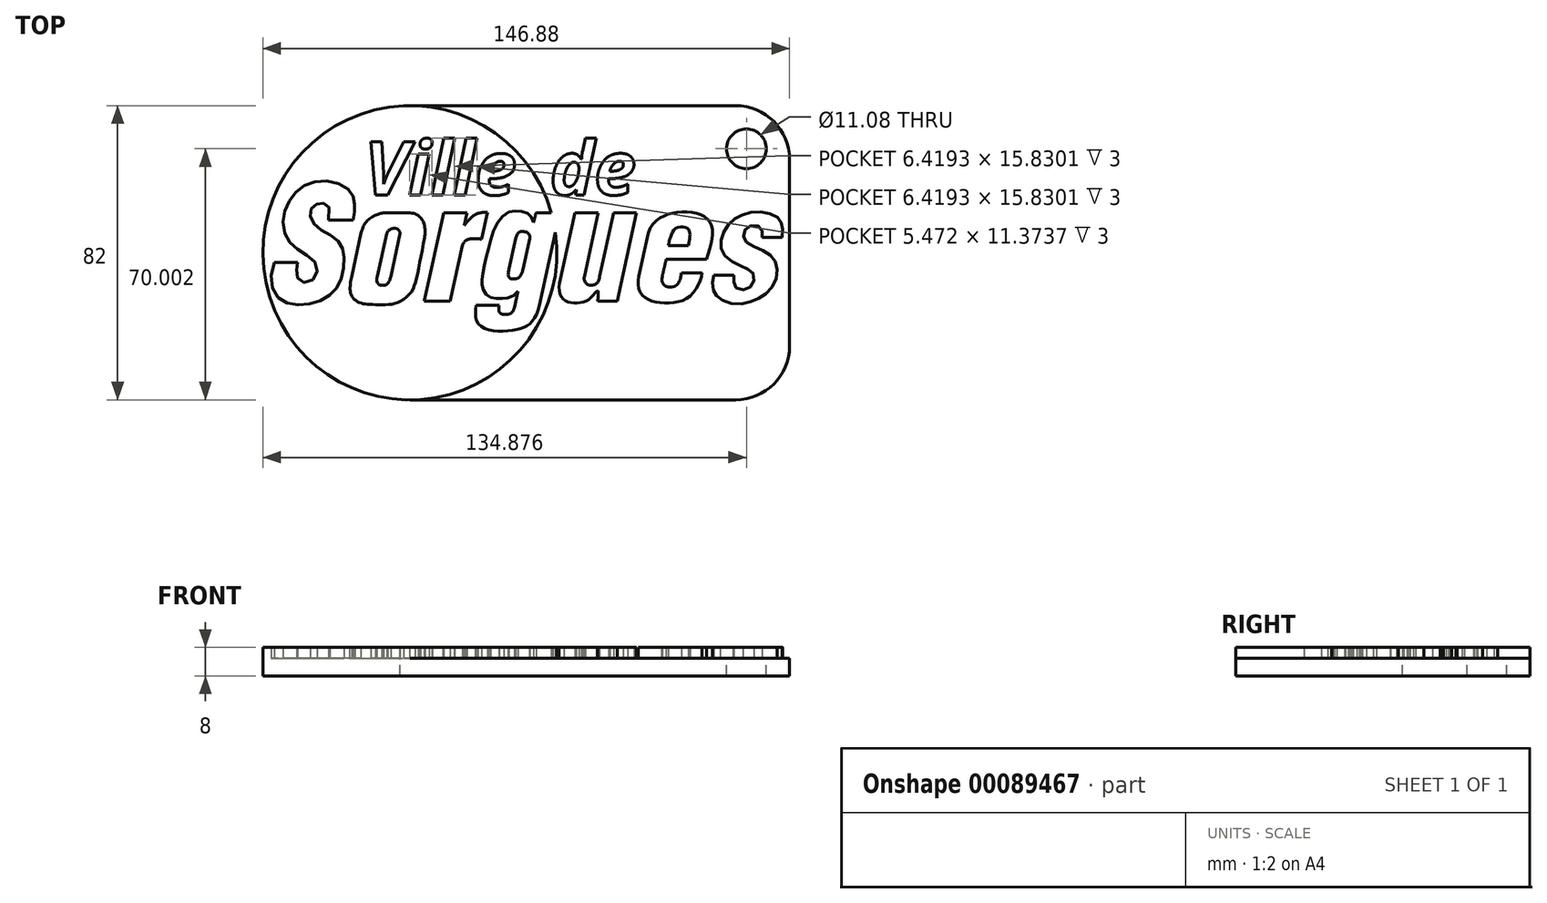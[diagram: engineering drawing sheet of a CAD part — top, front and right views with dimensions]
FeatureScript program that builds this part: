
annotation { "Feature Type Name" : "Feature", "Feature Type Description" : "" }
export const myFeature = defineFeature(function(context is Context, id is Id, definition is map)
    precondition{}
    {
        {
            var Q0;
            Q0=qCreatedBy(makeId("Top.planeOp"),FACE);
            var sketch = newSketch(context, id + "F0", { "sketchPlane" : qUnion([Q0])});
            skCircle(sketch, "E0", {"center": v(-30.87, 6.6) * mm, "radius": 41 * mm});
            skLineSegment(sketch, "E1", {"start": v(-46.68, 15.72) * mm, "end": v(-53.55, 15.72) * mm});
            skFitSpline(sketch, "E2", {"points": [v(-53.55, 15.72) * mm, v(-55.37, 20.45) * mm, v(-58.38, 18.72) * mm, v(-57.47, 14.47) * mm, v(-51.06, 10.07) * mm, v(-49.23, 4.58) * mm, v(-51.4, -3.41) * mm, v(-58.74, -7.62) * mm, v(-67.28, -6.17) * mm, v(-68.7, 3.91) * mm], "startDerivative": vector(30.5, 116.33) * mm, "endDerivative": vector(37.1, 85.72) * mm});
            skFitSpline(sketch, "E3", {"points": [v(-62.2, 3.91) * mm, v(-62.44, 1.12) * mm, v(-61.32, -1.4) * mm, v(-57.63, -0.75) * mm, v(-57.02, 3.45) * mm, v(-61, 6.77) * mm, v(-64.78, 10.13) * mm, v(-66.22, 15.64) * mm, v(-64.36, 21.2) * mm, v(-60.67, 25.07) * mm, v(-54.78, 26.66) * mm, v(-48.53, 24.7) * mm, v(-46.51, 21.77) * mm, v(-46.24, 18.72) * mm, v(-46.68, 15.72) * mm], "startDerivative": vector(-8.44, -44.96) * mm, "endDerivative": vector(-12.62, -61.68) * mm});
            skLineSegment(sketch, "E4", {"start": v(-68.7, 3.91) * mm, "end": v(-62.2, 3.91) * mm});
            skFitSpline(sketch, "E5", {"points": [v(-44.48, 12.03) * mm, v(-41.97, 16.18) * mm, v(-39.42, 17.46) * mm, v(-37.1, 17.75) * mm], "startDerivative": vector(4.21, 16.77) * mm, "endDerivative": vector(10.42, 0) * mm});
            skLineSegment(sketch, "E6", {"start": v(-44.48, 12.03) * mm, "end": v(-47.1, 0) * mm});
            skFitSpline(sketch, "E7", {"points": [v(-47.1, 0) * mm, v(-47.52, -2.89) * mm, v(-47.1, -5.39) * mm, v(-44.86, -7.3) * mm, v(-40.48, -7.86) * mm], "startDerivative": vector(-2.9, -11.48) * mm, "endDerivative": vector(16.85, 0) * mm});
            skLineSegment(sketch, "E8", {"start": v(-37.1, 17.75) * mm, "end": v(-31.46, 17.75) * mm});
            skFitSpline(sketch, "E9", {"points": [v(-31.46, 17.75) * mm, v(-28.52, 16.96) * mm, v(-27.19, 15.35) * mm, v(-26.63, 12.9) * mm, v(-26.77, 10.94) * mm], "startDerivative": vector(16.23, 0) * mm, "endDerivative": vector(-1.15, -8.28) * mm});
            skFitSpline(sketch, "E10", {"points": [v(-40.48, -7.86) * mm, v(-36.84, -7.86) * mm, v(-33.76, -7.04) * mm, v(-30.62, -4.52) * mm, v(-29, -0.53) * mm, v(-26.77, 10.94) * mm], "startDerivative": vector(21.93, -0.87) * mm, "endDerivative": vector(7.65, 42.34) * mm});
            skLineSegment(sketch, "E11", {"start": v(-39.95, 0) * mm, "end": v(-37.33, 12.03) * mm});
            skLineSegment(sketch, "E12", {"start": v(-33.58, 12.03) * mm, "end": v(-36.2, 0) * mm});
            skFitSpline(sketch, "E13", {"points": [v(-37.33, 12.03) * mm, v(-35.63, 13.36) * mm, v(-34.25, 13.16) * mm, v(-33.58, 12.03) * mm, v(-34.59, 11.23) * mm], "startDerivative": vector(4.06, 9.82) * mm, "endDerivative": vector(-5.98, -2.84) * mm});
            skFitSpline(sketch, "E14", {"points": [v(-39.95, 0) * mm, v(-39.5, -2.22) * mm, v(-37.71, -2.37) * mm, v(-36.65, -1.41) * mm, v(-36.2, 0) * mm], "startDerivative": vector(-2.91, -13) * mm, "endDerivative": vector(2.14, 8.95) * mm});
            skLineSegment(sketch, "E15", {"start": v(-26.8, -6.84) * mm, "end": v(-21.45, 17.75) * mm});
            skLineSegment(sketch, "E16", {"start": v(-21.45, 17.75) * mm, "end": v(-14.91, 17.75) * mm});
            skLineSegment(sketch, "E17", {"start": v(-14.91, 17.75) * mm, "end": v(-15.68, 14.23) * mm});
            skLineSegment(sketch, "E18", {"start": v(-26.8, -6.84) * mm, "end": v(-19.58, -6.84) * mm});
            skLineSegment(sketch, "E19", {"start": v(-19.58, -6.84) * mm, "end": v(-16.19, 8.72) * mm});
            skLineSegment(sketch, "E20", {"start": v(-10.86, 10.4) * mm, "end": v(-9.23, 17.89) * mm});
            skFitSpline(sketch, "E21", {"points": [v(-15.68, 14.23) * mm, v(-13.66, 16.46) * mm, v(-11.76, 17.62) * mm, v(-9.23, 17.89) * mm], "startDerivative": vector(5.4, 7.42) * mm, "endDerivative": vector(8.1, 0.22) * mm});
            skFitSpline(sketch, "E22", {"points": [v(-16.19, 8.72) * mm, v(-14.96, 10.15) * mm, v(-12.9, 10.55) * mm, v(-10.86, 10.4) * mm], "startDerivative": vector(3.02, 5.92) * mm, "endDerivative": vector(6.03, -0.64) * mm});
            skLineSegment(sketch, "E23", {"start": v(-3.2, 2.04) * mm, "end": v(-1.33, 10.61) * mm});
            skLineSegment(sketch, "E24", {"start": v(0.7, 2.04) * mm, "end": v(2.57, 10.61) * mm});
            skLineSegment(sketch, "E25", {"start": v(-0.74, -4.05) * mm, "end": v(-1.78, -8.83) * mm});
            skLineSegment(sketch, "E26", {"start": v(-12.33, -8) * mm, "end": v(-5.95, -8) * mm});
            skLineSegment(sketch, "E27", {"start": v(4.33, 17.75) * mm, "end": v(10.93, 17.75) * mm});
            skLineSegment(sketch, "E28", {"start": v(5.3, -8.04) * mm, "end": v(10.93, 17.75) * mm});
            skFitSpline(sketch, "E29", {"points": [v(-1.33, 10.61) * mm, v(-0.46, 12.23) * mm, v(0.86, 12.5) * mm, v(2.15, 12) * mm, v(2.59, 11.3) * mm, v(2.57, 10.61) * mm], "startDerivative": vector(1.37, 8.18) * mm, "endDerivative": vector(-0.73, -5.78) * mm});
            skFitSpline(sketch, "E30", {"points": [v(-3.2, 2.04) * mm, v(-3.44, 0.57) * mm, v(-3.2, -0.27) * mm, v(-2.17, -0.7) * mm, v(-0.65, -0.45) * mm, v(0.16, 0.48) * mm, v(0.4, 1.08) * mm, v(0.7, 2.04) * mm], "startDerivative": vector(-1.15, -6.79) * mm, "endDerivative": vector(2.21, 10.53) * mm});
            skFitSpline(sketch, "E31", {"points": [v(3.62, 15.02) * mm, v(2.53, 17.2) * mm, v(0, 18.19) * mm, v(-3.05, 18) * mm, v(-6.5, 14.88) * mm, v(-8.72, 8.69) * mm, v(-10.1, 3.25) * mm, v(-10.75, -0.82) * mm, v(-10.61, -2.76) * mm, v(-9.79, -4.72) * mm, v(-8.01, -5.97) * mm, v(-5.46, -6.16) * mm, v(-3.18, -5.86) * mm, v(-0.74, -4.05) * mm, v(-0.54, -3.09) * mm], "startDerivative": vector(-11.94, 38.07) * mm, "endDerivative": vector(-16.26, -31.54) * mm});
            skFitSpline(sketch, "E32", {"points": [v(-5.95, -8) * mm, v(-5.65, -10.26) * mm, v(-2.62, -10.2) * mm, v(-1.78, -8.83) * mm], "startDerivative": vector(-0.6, -8.06) * mm, "endDerivative": vector(1.49, 4.6) * mm});
            skFitSpline(sketch, "E33", {"points": [v(-12.33, -8) * mm, v(-12.33, -12.1) * mm, v(-9.84, -14.59) * mm, v(-3.98, -15.22) * mm, v(0.78, -14.25) * mm, v(3.2, -12.62) * mm, v(5.3, -8.04) * mm], "startDerivative": vector(-3.82, -23) * mm, "endDerivative": vector(7.38, 32.85) * mm});
            skFitSpline(sketch, "E34", {"points": [v(3.62, 15.02) * mm, v(4.33, 17.75) * mm], "startDerivative": vector(0.71, 2.5) * mm, "endDerivative": vector(0.71, 2.5) * mm});
            skPoint(sketch, "E35.orphan", {"position": v(11.99, 17.75) * mm});
            skLineSegment(sketch, "E36", {"start": v(15.2, 17.75) * mm, "end": v(21.67, 17.75) * mm});
            skPoint(sketch, "E36.startSnap0", {"position": v(7.63, 17.75) * mm});
            skLineSegment(sketch, "E37", {"start": v(25.94, 17.75) * mm, "end": v(32.3, 17.75) * mm});
            skLineSegment(sketch, "E38", {"start": v(21.5, -6.84) * mm, "end": v(26.94, -6.84) * mm});
            skPoint(sketch, "E38.startSnap0", {"position": v(-23.2, -6.84) * mm});
            skPoint(sketch, "E38.endSnap0", {"position": v(-23.2, -6.84) * mm});
            skLineSegment(sketch, "E39", {"start": v(40.62, 4.75) * mm, "end": v(51.92, 4.75) * mm});
            skLineSegment(sketch, "E40", {"start": v(41.22, 8.6) * mm, "end": v(46.8, 8.6) * mm});
            skLineSegment(sketch, "E41", {"start": v(15.2, 17.75) * mm, "end": v(10.91, -1.96) * mm});
            skLineSegment(sketch, "E42", {"start": v(21.67, 17.75) * mm, "end": v(17.8, 0) * mm});
            skLineSegment(sketch, "E43", {"start": v(25.94, 17.75) * mm, "end": v(22.07, 0) * mm});
            skLineSegment(sketch, "E44", {"start": v(32.3, 17.75) * mm, "end": v(26.94, -6.84) * mm});
            skLineSegment(sketch, "E45", {"start": v(35.56, 12.03) * mm, "end": v(32.94, 0) * mm});
            skFitSpline(sketch, "E46", {"points": [v(10.91, -1.96) * mm, v(11.94, -6.38) * mm, v(15.88, -7.4) * mm, v(19.48, -6.04) * mm, v(21.49, -4.03) * mm, v(21.5, -6.84) * mm], "startDerivative": vector(-4.87, -23.72) * mm, "endDerivative": vector(-3.5, -25.24) * mm});
            skFitSpline(sketch, "E47", {"points": [v(17.8, 0) * mm, v(18.89, -2.31) * mm, v(21.01, -2.1) * mm, v(22.07, 0) * mm], "startDerivative": vector(-2.23, -9) * mm, "endDerivative": vector(2.64, 10.78) * mm});
            skFitSpline(sketch, "E48", {"points": [v(35.56, 12.03) * mm, v(38.42, 15.94) * mm, v(41.6, 17.5) * mm, v(46.13, 18.02) * mm, v(50.22, 17.24) * mm, v(52.65, 15.32) * mm, v(53.55, 12.03) * mm, v(51.92, 4.75) * mm], "startDerivative": vector(8, 35.37) * mm, "endDerivative": vector(-6.52, -21.66) * mm});
            skFitSpline(sketch, "E49", {"points": [v(32.94, 0) * mm, v(34.12, -5.4) * mm, v(39.94, -7.4) * mm, v(47.3, -5.45) * mm, v(50.64, 0.91) * mm, v(50.68, 3.2) * mm], "startDerivative": vector(-6.28, -31.9) * mm, "endDerivative": vector(-0.94, 14.05) * mm});
            skFitSpline(sketch, "E50", {"points": [v(39.5, 0) * mm, v(40.62, -2.78) * mm, v(43.55, -2.4) * mm, v(44.67, 0) * mm, v(44.82, 0.91) * mm], "startDerivative": vector(-3.13, -15.6) * mm, "endDerivative": vector(0.96, 6.1) * mm});
            skFitSpline(sketch, "E51", {"points": [v(41.22, 8.6) * mm, v(41.58, 10.16) * mm, v(43.3, 13.38) * mm, v(46.58, 13.3) * mm, v(47.25, 11.6) * mm, v(46.8, 8.6) * mm], "startDerivative": vector(3.23, 15.78) * mm, "endDerivative": vector(-3.17, -15.13) * mm});
            skFitSpline(sketch, "E52", {"points": [v(40.62, 4.75) * mm, v(39.5, 0) * mm], "startDerivative": vector(-1.24, -4.75) * mm, "endDerivative": vector(-1.24, -4.75) * mm});
            skPoint(sketch, "E53.orphan", {"position": v(27.12, -6.84) * mm});
            skLineSegment(sketch, "E54", {"start": v(44.82, 0.91) * mm, "end": v(50.64, 0.91) * mm});
            skFitSpline(sketch, "E55", {"points": [v(67.4, 10.9) * mm, v(67.36, 12.7) * mm, v(66.34, 14.03) * mm, v(63.7, 13.96) * mm, v(62.34, 12.46) * mm, v(62.4, 10.4) * mm, v(64.15, 8.73) * mm, v(67.92, 7.05) * mm, v(70.48, 4.99) * mm, v(71.53, 2.32) * mm, v(71.04, -1.16) * mm, v(68.92, -4.37) * mm, v(66.03, -6.31) * mm, v(62.83, -7.42) * mm, v(58.16, -7.46) * mm, v(55.3, -5.98) * mm, v(54.07, -4.45) * mm, v(53.53, -2.15) * mm, v(53.96, 0.28) * mm], "startDerivative": vector(4.71, 40.9) * mm, "endDerivative": vector(10.6, 37.94) * mm});
            skFitSpline(sketch, "E56", {"points": [v(59.53, 0.4) * mm, v(59.46, -1.73) * mm, v(60.46, -3.38) * mm, v(63.13, -3.55) * mm, v(65, -1.75) * mm, v(64.82, 0.94) * mm, v(63.17, 2.17) * mm, v(59.68, 3.72) * mm, v(56.58, 6.31) * mm, v(55.81, 9.37) * mm, v(56.82, 12.78) * mm, v(59.03, 15.48) * mm, v(61.96, 17.2) * mm, v(66.03, 18) * mm, v(70.3, 17.15) * mm, v(72.36, 15.67) * mm, v(72.98, 13.88) * mm, v(72.95, 10.9) * mm], "startDerivative": vector(-8.42, -48.12) * mm, "endDerivative": vector(-7.47, -56.36) * mm});
            skLineSegment(sketch, "E57", {"start": v(53.96, 0.28) * mm, "end": v(59.51, 0.28) * mm});
            skLineSegment(sketch, "E58", {"start": v(67.4, 10.9) * mm, "end": v(72.95, 10.9) * mm});
            skLineSegment(sketch, "E59.bottom", {"start": v(-30.87, 47.6) * mm, "end": v(75, 47.6) * mm});
            skLineSegment(sketch, "E59.top", {"start": v(-30.87, -34.4) * mm, "end": v(75, -34.4) * mm});
            skLineSegment(sketch, "E59.right", {"start": v(75, 47.6) * mm, "end": v(75, -34.4) * mm});
            skCircle(sketch, "E60", {"center": v(63, 35.6) * mm, "radius": 5.54 * mm});
            skSolve(sketch);
        }
        {
            var Q0;
            Q0=qCreatedBy(makeId("Top.planeOp"),FACE);
            var sketch = newSketch(context, id + "F1", { "sketchPlane" : qUnion([Q0])});
            skText(sketch, "E61", { "text": "Ville", "fontName": "OpenSans-BoldItalic.ttf"});
            const initialGuessF1  = {"E61": [-0.04358, 0.02272, 1, 0, 0.015]};
            skSetInitialGuess(sketch, initialGuessF1);
            skSolve(sketch);
        }
        {
            var Q0;
            Q0=qCreatedBy(makeId("Top.planeOp"),FACE);
            var sketch = newSketch(context, id + "F2", { "sketchPlane" : qUnion([Q0])});
            skText(sketch, "E62", { "text": "de", "fontName": "OpenSans-BoldItalic.ttf"});
            const initialGuessF2  = {"E62": [0.00816, 0.02275, 1, 0, 0.015]};
            skSetInitialGuess(sketch, initialGuessF2);
            skSolve(sketch);
        }
        {
            var Q0;
            Q0=makeQuery(id+"F0.imprint","IMPRINT",FACE,{"disambiguationData":[TD([[makeQuery(id+"F0.imprint","IMPRINT",EDGE,{"derivedFrom":sQuery(id+"F0.wireOp",EDGE,"E1")}),1.0]])]});
            var Q1;
            Q1=makeQuery(id+"F0.imprint","IMPRINT",FACE,{"disambiguationData":[TD([[makeQuery(id+"F0.imprint","IMPRINT",EDGE,{"derivedFrom":sQuery(id+"F0.wireOp",EDGE,"E36")}),1.0]])]});
            var Q2;
            Q2=makeQuery(id+"F0.imprint","IMPRINT",FACE,{"disambiguationData":[TD([[makeQuery(id+"F0.imprint","IMPRINT",EDGE,{"derivedFrom":sQuery(id+"F0.wireOp",EDGE,"E1")}),-1.0]])]});
            var Q3;
            Q3=makeQuery(id+"F0.imprint","IMPRINT",FACE,{"disambiguationData":[TD([[makeQuery(id+"F0.imprint","IMPRINT",EDGE,{"derivedFrom":sQuery(id+"F0.wireOp",EDGE,"E5")}),-1.0]])]});
            var Q4;
            {var subQ1=sQuery(id+"F0.wireOp",EDGE,"E11");Q4=makeQuery(id+"F0.imprint","IMPRINT",FACE,{"disambiguationData":[TD([[makeQuery(id+"F0.imprint","IMPRINT",EDGE,{"derivedFrom":subQ1}),-1.0]])]});}
            var Q5;
            Q5=makeQuery(id+"F0.imprint","IMPRINT",FACE,{"disambiguationData":[TD([[makeQuery(id+"F0.imprint","IMPRINT",EDGE,{"derivedFrom":sQuery(id+"F0.wireOp",EDGE,"E15")}),-1.0]])]});
            var Q6;
            Q6=makeQuery(id+"F0.imprint","IMPRINT",FACE,{"disambiguationData":[TD([[makeQuery(id+"F0.imprint","IMPRINT",EDGE,{"derivedFrom":sQuery(id+"F0.wireOp",EDGE,"E23")}),1.0]])]});
            var Q7;
            Q7=makeQuery(id+"F0.imprint","IMPRINT",FACE,{"disambiguationData":[TD([[makeQuery(id+"F0.imprint","IMPRINT",EDGE,{"derivedFrom":sQuery(id+"F0.wireOp",EDGE,"E23")}),-1.0]])]});
            var Q8;
            {var subQ0=sQuery(id+"F0.wireOp",EDGE,"E27");var subQ1=sQuery(id+"F0.wireOp",EDGE,"E0");var subQ2=makeQuery(id+"F0.imprint","INTERSECT",VERTEX,{"derivedFrom":[subQ1,subQ0]});Q8=makeQuery(id+"F0.imprint","IMPRINT",FACE,{"disambiguationData":[TD([[makeQuery(id+"F0.imprint","IMPRINT",EDGE,{"disambiguationData":[TD([[subQ2,1.0]])],"derivedFrom":subQ1}),-1.0]])]});}
            var Q9;
            Q9=makeQuery(id+"F0.imprint","IMPRINT",FACE,{"disambiguationData":[TD([[makeQuery(id+"F0.imprint","IMPRINT",EDGE,{"derivedFrom":sQuery(id+"F0.wireOp",EDGE,"E36")}),-1.0]])]});
            var Q10;
            Q10=makeQuery(id+"F0.imprint","IMPRINT",FACE,{"disambiguationData":[TD([[makeQuery(id+"F0.imprint","IMPRINT",EDGE,{"derivedFrom":sQuery(id+"F0.wireOp",EDGE,"E39")}),1.0]])]});
            var Q11;
            Q11=makeQuery(id+"F0.imprint","IMPRINT",FACE,{"disambiguationData":[TD([[makeQuery(id+"F0.imprint","IMPRINT",EDGE,{"derivedFrom":sQuery(id+"F0.wireOp",EDGE,"E40")}),1.0]])]});
            var Q12;
            Q12=makeQuery(id+"F0.imprint","IMPRINT",FACE,{"disambiguationData":[TD([[makeQuery(id+"F0.imprint","IMPRINT",EDGE,{"derivedFrom":sQuery(id+"F0.wireOp",EDGE,"E55")}),-1.0]])]});
            extrude(context, id + "F3", {"entities" : qUnion([Q0, Q1, Q2, Q3, Q4, Q5, Q6, Q7, Q8, Q9, Q10, Q11, Q12]), "oppositeDirection" : true, "depth" : 5 * mm});
        }
        {
            var Q0;
            Q0=makeQuery(id+"F0.imprint","IMPRINT",FACE,{"disambiguationData":[TD([[makeQuery(id+"F0.imprint","IMPRINT",EDGE,{"derivedFrom":sQuery(id+"F0.wireOp",EDGE,"E1")}),1.0]])]});
            var Q1;
            {var subQ1=sQuery(id+"F0.wireOp",EDGE,"E11");Q1=makeQuery(id+"F0.imprint","IMPRINT",FACE,{"disambiguationData":[TD([[makeQuery(id+"F0.imprint","IMPRINT",EDGE,{"derivedFrom":subQ1}),-1.0]])]});}
            var Q2;
            Q2=makeQuery(id+"F0.imprint","IMPRINT",FACE,{"disambiguationData":[TD([[makeQuery(id+"F0.imprint","IMPRINT",EDGE,{"derivedFrom":sQuery(id+"F0.wireOp",EDGE,"E23")}),-1.0]])]});
            var Q3;
            Q3 = qSketchRegion(id + "F2", true);
            var Q4;
            Q4=makeQuery(id+"F0.imprint","IMPRINT",FACE,{"disambiguationData":[TD([[makeQuery(id+"F0.imprint","IMPRINT",EDGE,{"derivedFrom":sQuery(id+"F0.wireOp",EDGE,"E36")}),-1.0]])]});
            var Q5;
            Q5=makeQuery(id+"F0.imprint","IMPRINT",FACE,{"disambiguationData":[TD([[makeQuery(id+"F0.imprint","IMPRINT",EDGE,{"derivedFrom":sQuery(id+"F0.wireOp",EDGE,"E39")}),1.0]])]});
            var Q6;
            Q6=makeQuery(id+"F0.imprint","IMPRINT",FACE,{"disambiguationData":[TD([[makeQuery(id+"F0.imprint","IMPRINT",EDGE,{"derivedFrom":sQuery(id+"F0.wireOp",EDGE,"E55")}),-1.0]])]});
            extrude(context, id + "F4", {"entities" : qUnion([Q0, Q1, Q2, Q3, Q4, Q5, Q6]), "operationType" : NewBodyOperationType.ADD, "depth" : 3 * mm});
        }
        {
            var Q0;
            Q0 = qSketchRegion(id + "F1", true);
            extrude(context, id + "F5", {"entities" : qUnion([Q0]), "operationType" : NewBodyOperationType.REMOVE, "depth" : 25 * mm});
        }
        {
            var Q0;
            Q0=makeQuery(id+"F3.opExtrude","SWEPT_EDGE",EDGE,{"disambiguationData":[OSD([sQuery(id+"F0.wireOp",EDGE,"E59.bottom"),sQuery(id+"F0.wireOp",EDGE,"E59.right")])]});
            var Q1;
            Q1=makeQuery(id+"F3.opExtrude","SWEPT_EDGE",EDGE,{"disambiguationData":[OSD([sQuery(id+"F0.wireOp",EDGE,"E59.top"),sQuery(id+"F0.wireOp",EDGE,"E59.right")])]});
            fillet(context, id + "F6", {"entities" : qUnion([Q0, Q1]), "radius" : 15 * mm, "tangentPropagation" : true, "allowEdgeOverflow" : false});
        }
    });
